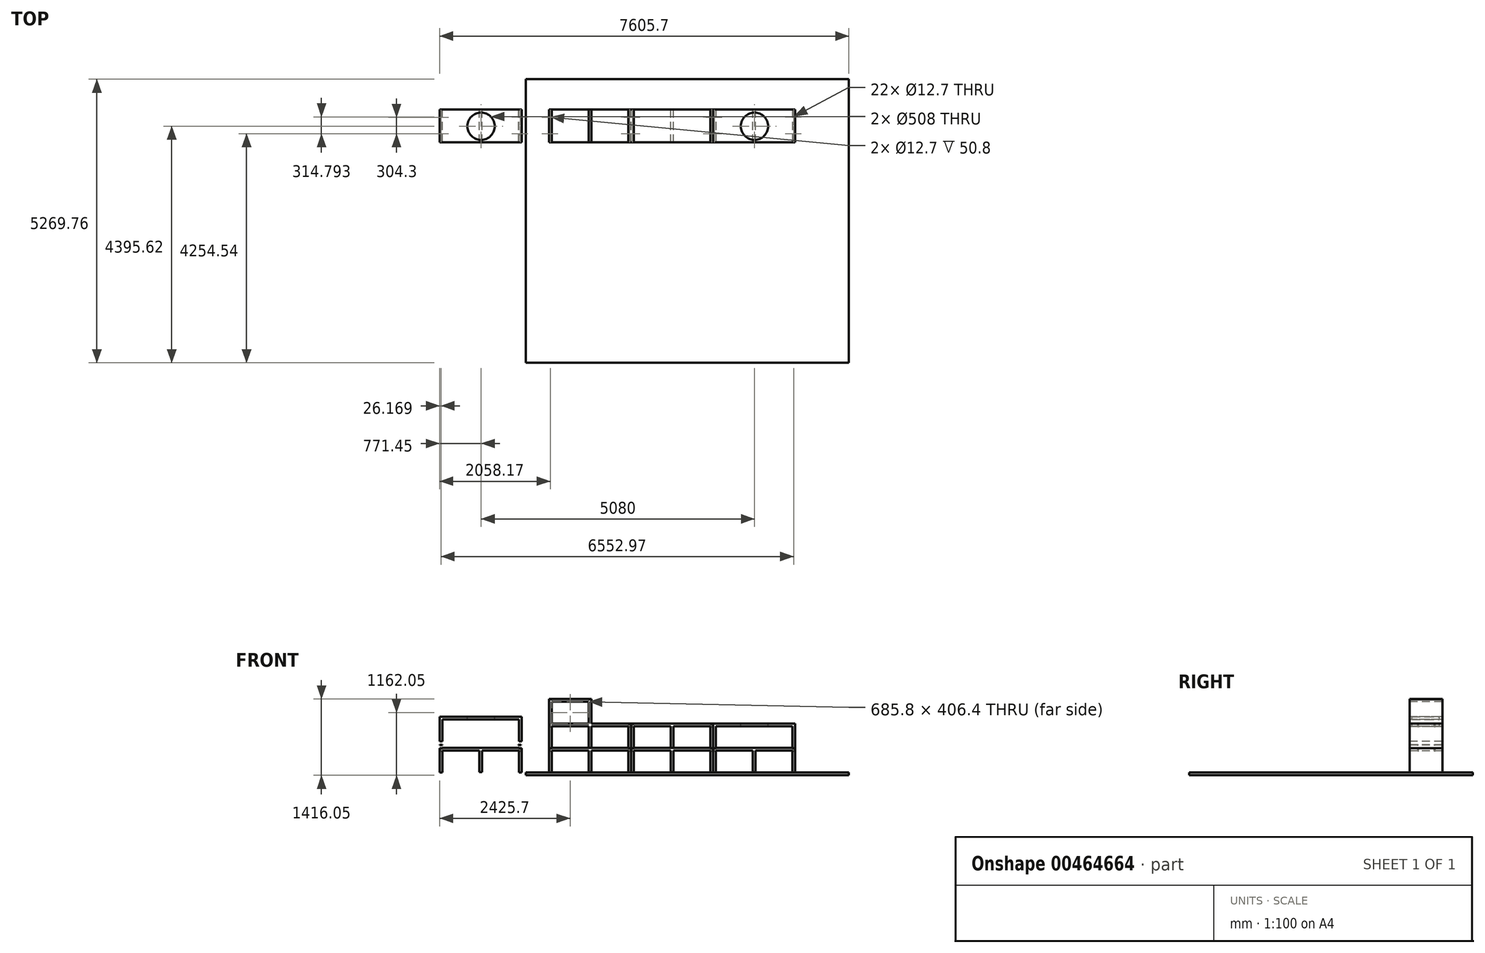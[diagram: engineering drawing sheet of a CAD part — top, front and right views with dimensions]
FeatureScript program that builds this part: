
annotation { "Feature Type Name" : "Feature", "Feature Type Description" : "" }
export const myFeature = defineFeature(function(context is Context, id is Id, definition is map)
    precondition{}
    {
        {
            var Q0;
            Q0=qCreatedBy(makeId("Front.planeOp"),FACE);
            var sketch = newSketch(context, id + "F0", { "sketchPlane" : qUnion([Q0])});
            skLineSegment(sketch, "E0", {"start": v(-136.8, -22.2) * mm, "end": v(-136.8, 33.81) * mm});
            skLineSegment(sketch, "E1", {"start": v(-110.83, 105.81) * mm, "end": v(-110.83, 556.66) * mm});
            skLineSegment(sketch, "E2", {"start": v(-110.83, 556.66) * mm, "end": v(-60.03, 556.66) * mm});
            skLineSegment(sketch, "E3", {"start": v(-60.03, 556.66) * mm, "end": v(-60.03, 563.01) * mm});
            skLineSegment(sketch, "E4", {"start": v(-60.03, 563.01) * mm, "end": v(1362.37, 563.01) * mm});
            skLineSegment(sketch, "E5", {"start": v(1362.37, 563.01) * mm, "end": v(1362.37, 556.66) * mm});
            skLineSegment(sketch, "E6", {"start": v(1362.37, 556.66) * mm, "end": v(1413.17, 556.66) * mm});
            skLineSegment(sketch, "E7", {"start": v(1413.17, 556.66) * mm, "end": v(1413.17, 105.81) * mm});
            skLineSegment(sketch, "E8", {"start": v(1413.17, 105.81) * mm, "end": v(1362.37, 105.81) * mm});
            skLineSegment(sketch, "E9", {"start": v(1362.37, 105.81) * mm, "end": v(1362.37, 512.21) * mm});
            skLineSegment(sketch, "E10", {"start": v(1362.37, 512.21) * mm, "end": v(676.57, 512.21) * mm});
            skLineSegment(sketch, "E11", {"start": v(676.57, 512.21) * mm, "end": v(676.57, 112.16) * mm});
            skLineSegment(sketch, "E12", {"start": v(676.57, 112.16) * mm, "end": v(625.77, 112.16) * mm});
            skLineSegment(sketch, "E13", {"start": v(625.77, 112.16) * mm, "end": v(625.77, 512.21) * mm});
            skLineSegment(sketch, "E14", {"start": v(625.77, 512.21) * mm, "end": v(-60.03, 512.21) * mm});
            skLineSegment(sketch, "E15", {"start": v(-60.03, 512.21) * mm, "end": v(-60.03, 105.81) * mm});
            skLineSegment(sketch, "E16", {"start": v(-60.03, 105.81) * mm, "end": v(-110.83, 105.81) * mm});
            skSolve(sketch);
        }
        {
            var Q0;
            Q0 = qSketchRegion(id + "F0", true);
            extrude(context, id + "F1", {"entities" : qUnion([Q0]), "depth" : 609.6 * mm});
        }
        {
            var Q0;
            Q0=makeQuery(id+"F1.opExtrude","SWEPT_FACE",FACE,{"disambiguationData":[OSD([sQuery(id+"F0.wireOp",EDGE,"E6")])]});
            var sketch = newSketch(context, id + "F2", { "sketchPlane" : qUnion([Q0])});
            skPoint(sketch, "E17", {"position": v(1388.3, -450.4) * mm});
            skPoint(sketch, "E18", {"position": v(1388.3, -135.6) * mm});
            skPoint(sketch, "E19", {"position": v(-84.66, -450.4) * mm});
            skPoint(sketch, "E20", {"position": v(-84.66, -146.1) * mm});
            skSolve(sketch);
        }
        {
            var Q0;
            Q0=sQuery(id+"F2.wireOp",VERTEX,"E20");
            var Q1;
            Q1=sQuery(id+"F2.wireOp",VERTEX,"E19");
            var Q2;
            Q2=sQuery(id+"F2.wireOp",VERTEX,"E18");
            var Q3;
            Q3=sQuery(id+"F2.wireOp",VERTEX,"E17");
            var Q4;
            Q4=makeQuery(id+"F1.opExtrude","SWEPT_BODY",BODY,{"disambiguationData":[OSD([sQuery(id+"F0.wireOp",EDGE,"E1"),sQuery(id+"F0.wireOp",EDGE,"E2"),sQuery(id+"F0.wireOp",EDGE,"E3"),sQuery(id+"F0.wireOp",EDGE,"E4"),sQuery(id+"F0.wireOp",EDGE,"E5"),sQuery(id+"F0.wireOp",EDGE,"E6"),sQuery(id+"F0.wireOp",EDGE,"E7"),sQuery(id+"F0.wireOp",EDGE,"E8"),sQuery(id+"F0.wireOp",EDGE,"E9"),sQuery(id+"F0.wireOp",EDGE,"E10"),sQuery(id+"F0.wireOp",EDGE,"E11"),sQuery(id+"F0.wireOp",EDGE,"E12"),sQuery(id+"F0.wireOp",EDGE,"E13"),sQuery(id+"F0.wireOp",EDGE,"E14"),sQuery(id+"F0.wireOp",EDGE,"E15"),sQuery(id+"F0.wireOp",EDGE,"E16")])]});
            hole(context, id + "F3", {"style" : HoleStyle.SIMPLE, "endStyle" : HoleEndStyle.BLIND, "holeDiameter" : 12.7 * mm, "holeDepth" : 50.8 * mm, "isTappedThrough" : true, "tappedDepth" : 12.7 * mm, "tapClearance" : 3, "locations" : qUnion([Q0, Q1, Q2, Q3]), "scope" : qUnion([Q4])});
        }
        {
            var Q0;
            Q0=makeQuery(id+"F1.opExtrude","CAP_FACE",FACE,{"disambiguationData":[OSD([sQuery(id+"F0.wireOp",EDGE,"E1"),sQuery(id+"F0.wireOp",EDGE,"E2"),sQuery(id+"F0.wireOp",EDGE,"E3"),sQuery(id+"F0.wireOp",EDGE,"E4"),sQuery(id+"F0.wireOp",EDGE,"E5"),sQuery(id+"F0.wireOp",EDGE,"E6"),sQuery(id+"F0.wireOp",EDGE,"E7"),sQuery(id+"F0.wireOp",EDGE,"E8"),sQuery(id+"F0.wireOp",EDGE,"E9"),sQuery(id+"F0.wireOp",EDGE,"E10"),sQuery(id+"F0.wireOp",EDGE,"E11"),sQuery(id+"F0.wireOp",EDGE,"E12"),sQuery(id+"F0.wireOp",EDGE,"E13"),sQuery(id+"F0.wireOp",EDGE,"E14"),sQuery(id+"F0.wireOp",EDGE,"E15"),sQuery(id+"F0.wireOp",EDGE,"E16")])],"isStart":false});
            var sketch = newSketch(context, id + "F4", { "sketchPlane" : qUnion([Q0])});
            skLineSegment(sketch, "E21.bottom", {"start": v(-60.03, 614.6) * mm, "end": v(-110.83, 614.6) * mm});
            skLineSegment(sketch, "E21.top", {"start": v(-60.03, 620.95) * mm, "end": v(-110.83, 620.95) * mm});
            skLineSegment(sketch, "E21.left", {"start": v(-60.03, 614.6) * mm, "end": v(-60.03, 620.95) * mm});
            skLineSegment(sketch, "E21.right", {"start": v(-110.83, 614.6) * mm, "end": v(-110.83, 620.95) * mm});
            skLineSegment(sketch, "E22.bottom", {"start": v(1354.2, 620.95) * mm, "end": v(1405, 620.95) * mm});
            skLineSegment(sketch, "E22.top", {"start": v(1354.2, 614.6) * mm, "end": v(1405, 614.6) * mm});
            skLineSegment(sketch, "E22.left", {"start": v(1354.2, 620.95) * mm, "end": v(1354.2, 614.6) * mm});
            skLineSegment(sketch, "E22.right", {"start": v(1405, 620.95) * mm, "end": v(1405, 614.6) * mm});
            skSolve(sketch);
        }
        {
            var Q0;
            Q0 = qSketchRegion(id + "F4", true);
            extrude(context, id + "F5", {"entities" : qUnion([Q0]), "depth" : -609.6 * mm});
        }
        {
            var Q0;
            Q0=makeQuery(id+"F5.opExtrude","SWEPT_FACE",FACE,{"disambiguationData":[OSD([sQuery(id+"F4.wireOp",EDGE,"E21.top")])]});
            var sketch = newSketch(context, id + "F6", { "sketchPlane" : qUnion([Q0])});
            skPoint(sketch, "E23", {"position": v(-84.4, -137.65) * mm});
            skPoint(sketch, "E24", {"position": v(-84.4, -453.82) * mm});
            skSolve(sketch);
        }
        {
            var Q0;
            Q0=sQuery(id+"F6.wireOp",VERTEX,"E23");
            var Q1;
            Q1=sQuery(id+"F6.wireOp",VERTEX,"E24");
            var Q2;
            Q2=makeQuery(id+"F5.opExtrude","SWEPT_BODY",BODY,{"disambiguationData":[OSD([sQuery(id+"F4.wireOp",EDGE,"E21.bottom"),sQuery(id+"F4.wireOp",EDGE,"E21.top"),sQuery(id+"F4.wireOp",EDGE,"E21.left"),sQuery(id+"F4.wireOp",EDGE,"E21.right")])]});
            hole(context, id + "F7", {"style" : HoleStyle.SIMPLE, "endStyle" : HoleEndStyle.BLIND, "holeDiameter" : 6.35 * mm, "holeDepth" : 6.35 * mm, "isTappedThrough" : true, "tappedDepth" : 12.7 * mm, "tapClearance" : 3, "locations" : qUnion([Q0, Q1]), "scope" : qUnion([Q2])});
        }
        {
            var Q0;
            Q0=makeQuery(id+"F5.opExtrude","SWEPT_FACE",FACE,{"disambiguationData":[OSD([sQuery(id+"F4.wireOp",EDGE,"E22.bottom")])]});
            var sketch = newSketch(context, id + "F8", { "sketchPlane" : qUnion([Q0])});
            skPoint(sketch, "E25", {"position": v(1380.3, -144.1) * mm});
            skPoint(sketch, "E26", {"position": v(1380.3, -466.73) * mm});
            skSolve(sketch);
        }
        {
            var Q0;
            Q0=sQuery(id+"F8.wireOp",VERTEX,"E25");
            var Q1;
            Q1=sQuery(id+"F8.wireOp",VERTEX,"E26");
            var Q2;
            Q2=makeQuery(id+"F5.opExtrude","SWEPT_BODY",BODY,{"disambiguationData":[OSD([sQuery(id+"F4.wireOp",EDGE,"E22.bottom"),sQuery(id+"F4.wireOp",EDGE,"E22.top"),sQuery(id+"F4.wireOp",EDGE,"E22.left"),sQuery(id+"F4.wireOp",EDGE,"E22.right")])]});
            hole(context, id + "F9", {"style" : HoleStyle.SIMPLE, "endStyle" : HoleEndStyle.BLIND, "holeDiameter" : 6.35 * mm, "holeDepth" : 6.35 * mm, "isTappedThrough" : true, "tappedDepth" : 12.7 * mm, "tapClearance" : 3, "locations" : qUnion([Q0, Q1]), "scope" : qUnion([Q2])});
        }
        {
            var Q0;
            Q0=makeQuery(id+"F1.opExtrude","CAP_FACE",FACE,{"disambiguationData":[OSD([sQuery(id+"F0.wireOp",EDGE,"E1"),sQuery(id+"F0.wireOp",EDGE,"E2"),sQuery(id+"F0.wireOp",EDGE,"E3"),sQuery(id+"F0.wireOp",EDGE,"E4"),sQuery(id+"F0.wireOp",EDGE,"E5"),sQuery(id+"F0.wireOp",EDGE,"E6"),sQuery(id+"F0.wireOp",EDGE,"E7"),sQuery(id+"F0.wireOp",EDGE,"E8"),sQuery(id+"F0.wireOp",EDGE,"E9"),sQuery(id+"F0.wireOp",EDGE,"E10"),sQuery(id+"F0.wireOp",EDGE,"E11"),sQuery(id+"F0.wireOp",EDGE,"E12"),sQuery(id+"F0.wireOp",EDGE,"E13"),sQuery(id+"F0.wireOp",EDGE,"E14"),sQuery(id+"F0.wireOp",EDGE,"E15"),sQuery(id+"F0.wireOp",EDGE,"E16")])],"isStart":false});
            var sketch = newSketch(context, id + "F10", { "sketchPlane" : qUnion([Q0])});
            skLineSegment(sketch, "E27", {"start": v(-110.83, 683.85) * mm, "end": v(-110.83, 1141.05) * mm});
            skLineSegment(sketch, "E28", {"start": v(-110.83, 1141.05) * mm, "end": v(1413.17, 1141.05) * mm});
            skLineSegment(sketch, "E29", {"start": v(1413.17, 1141.05) * mm, "end": v(1413.17, 683.85) * mm});
            skLineSegment(sketch, "E30", {"start": v(1413.17, 683.85) * mm, "end": v(1362.37, 683.85) * mm});
            skLineSegment(sketch, "E31", {"start": v(1362.37, 683.85) * mm, "end": v(1362.37, 1090.25) * mm});
            skLineSegment(sketch, "E32", {"start": v(1362.37, 1090.25) * mm, "end": v(-60.03, 1090.25) * mm});
            skLineSegment(sketch, "E33", {"start": v(-60.03, 1090.25) * mm, "end": v(-60.03, 683.85) * mm});
            skLineSegment(sketch, "E34", {"start": v(-60.03, 683.85) * mm, "end": v(-110.83, 683.85) * mm});
            skSolve(sketch);
        }
        {
            var Q0;
            Q0 = qSketchRegion(id + "F10", true);
            extrude(context, id + "F11", {"entities" : qUnion([Q0]), "depth" : -609.6 * mm});
        }
        {
            var Q0;
            Q0=makeQuery(id+"F11.opExtrude","SWEPT_FACE",FACE,{"disambiguationData":[OSD([sQuery(id+"F10.wireOp",EDGE,"E28")])]});
            var sketch = newSketch(context, id + "F12", { "sketchPlane" : qUnion([Q0])});
            skPoint(sketch, "E35", {"position": v(660.62, -309.31) * mm});
            skSolve(sketch);
        }
        {
            var Q0;
            Q0=sQuery(id+"F12.wireOp",VERTEX,"E35");
            var Q1;
            Q1=makeQuery(id+"F11.opExtrude","SWEPT_BODY",BODY,{"disambiguationData":[OSD([sQuery(id+"F10.wireOp",EDGE,"E27"),sQuery(id+"F10.wireOp",EDGE,"E28"),sQuery(id+"F10.wireOp",EDGE,"E29"),sQuery(id+"F10.wireOp",EDGE,"E30"),sQuery(id+"F10.wireOp",EDGE,"E31"),sQuery(id+"F10.wireOp",EDGE,"E32"),sQuery(id+"F10.wireOp",EDGE,"E33"),sQuery(id+"F10.wireOp",EDGE,"E34")])]});
            hole(context, id + "F13", {"style" : HoleStyle.SIMPLE, "endStyle" : HoleEndStyle.BLIND, "holeDiameter" : 508 * mm, "holeDepth" : 50.8 * mm, "isTappedThrough" : true, "tappedDepth" : 12.7 * mm, "tapClearance" : 3, "locations" : qUnion([Q0]), "scope" : qUnion([Q1])});
        }
        {
            var Q0;
            Q0=makeQuery(id+"F1.opExtrude","SWEPT_BODY",BODY,{"disambiguationData":[OSD([sQuery(id+"F0.wireOp",EDGE,"E1"),sQuery(id+"F0.wireOp",EDGE,"E2"),sQuery(id+"F0.wireOp",EDGE,"E3"),sQuery(id+"F0.wireOp",EDGE,"E4"),sQuery(id+"F0.wireOp",EDGE,"E5"),sQuery(id+"F0.wireOp",EDGE,"E6"),sQuery(id+"F0.wireOp",EDGE,"E7"),sQuery(id+"F0.wireOp",EDGE,"E8"),sQuery(id+"F0.wireOp",EDGE,"E9"),sQuery(id+"F0.wireOp",EDGE,"E10"),sQuery(id+"F0.wireOp",EDGE,"E11"),sQuery(id+"F0.wireOp",EDGE,"E12"),sQuery(id+"F0.wireOp",EDGE,"E13"),sQuery(id+"F0.wireOp",EDGE,"E14"),sQuery(id+"F0.wireOp",EDGE,"E15"),sQuery(id+"F0.wireOp",EDGE,"E16")])]});
            transform(context, id + "F14", {"entities" : qUnion([Q0]), "transformType" : TransformType.TRANSLATION_3D, "dx" : 2032 * mm, "dy" : 0 * mm, "dz" : 0 * mm, "makeCopy" : true});
        }
        {
            var Q0;
            Q0=makeQuery(id+"F14.opPattern","COPY",BODY,{"derivedFrom":makeQuery(id+"F1.opExtrude","SWEPT_BODY",BODY,{"disambiguationData":[OSD([sQuery(id+"F0.wireOp",EDGE,"E1"),sQuery(id+"F0.wireOp",EDGE,"E2"),sQuery(id+"F0.wireOp",EDGE,"E3"),sQuery(id+"F0.wireOp",EDGE,"E4"),sQuery(id+"F0.wireOp",EDGE,"E5"),sQuery(id+"F0.wireOp",EDGE,"E6"),sQuery(id+"F0.wireOp",EDGE,"E7"),sQuery(id+"F0.wireOp",EDGE,"E8"),sQuery(id+"F0.wireOp",EDGE,"E9"),sQuery(id+"F0.wireOp",EDGE,"E10"),sQuery(id+"F0.wireOp",EDGE,"E11"),sQuery(id+"F0.wireOp",EDGE,"E12"),sQuery(id+"F0.wireOp",EDGE,"E13"),sQuery(id+"F0.wireOp",EDGE,"E14"),sQuery(id+"F0.wireOp",EDGE,"E15"),sQuery(id+"F0.wireOp",EDGE,"E16")])]}),"instanceName":"1"});
            transform(context, id + "F15", {"entities" : qUnion([Q0]), "transformType" : TransformType.TRANSLATION_3D, "dx" : 0 * mm, "dy" : 0 * mm, "dz" : 450.85 * mm, "makeCopy" : true});
        }
        {
            var Q0;
            Q0=makeQuery(id+"F14.opPattern","COPY",BODY,{"derivedFrom":makeQuery(id+"F1.opExtrude","SWEPT_BODY",BODY,{"disambiguationData":[OSD([sQuery(id+"F0.wireOp",EDGE,"E1"),sQuery(id+"F0.wireOp",EDGE,"E2"),sQuery(id+"F0.wireOp",EDGE,"E3"),sQuery(id+"F0.wireOp",EDGE,"E4"),sQuery(id+"F0.wireOp",EDGE,"E5"),sQuery(id+"F0.wireOp",EDGE,"E6"),sQuery(id+"F0.wireOp",EDGE,"E7"),sQuery(id+"F0.wireOp",EDGE,"E8"),sQuery(id+"F0.wireOp",EDGE,"E9"),sQuery(id+"F0.wireOp",EDGE,"E10"),sQuery(id+"F0.wireOp",EDGE,"E11"),sQuery(id+"F0.wireOp",EDGE,"E12"),sQuery(id+"F0.wireOp",EDGE,"E13"),sQuery(id+"F0.wireOp",EDGE,"E14"),sQuery(id+"F0.wireOp",EDGE,"E15"),sQuery(id+"F0.wireOp",EDGE,"E16")])]}),"instanceName":"1"});
            transform(context, id + "F16", {"entities" : qUnion([Q0]), "transformType" : TransformType.TRANSLATION_3D, "dx" : 1524 * mm, "dy" : 0 * mm, "dz" : 0 * mm, "makeCopy" : true});
        }
        {
            var Q0;
            Q0=makeQuery(id+"F15.opPattern","COPY",BODY,{"derivedFrom":makeQuery(id+"F14.opPattern","COPY",BODY,{"derivedFrom":makeQuery(id+"F1.opExtrude","SWEPT_BODY",BODY,{"disambiguationData":[OSD([sQuery(id+"F0.wireOp",EDGE,"E1"),sQuery(id+"F0.wireOp",EDGE,"E2"),sQuery(id+"F0.wireOp",EDGE,"E3"),sQuery(id+"F0.wireOp",EDGE,"E4"),sQuery(id+"F0.wireOp",EDGE,"E5"),sQuery(id+"F0.wireOp",EDGE,"E6"),sQuery(id+"F0.wireOp",EDGE,"E7"),sQuery(id+"F0.wireOp",EDGE,"E8"),sQuery(id+"F0.wireOp",EDGE,"E9"),sQuery(id+"F0.wireOp",EDGE,"E10"),sQuery(id+"F0.wireOp",EDGE,"E11"),sQuery(id+"F0.wireOp",EDGE,"E12"),sQuery(id+"F0.wireOp",EDGE,"E13"),sQuery(id+"F0.wireOp",EDGE,"E14"),sQuery(id+"F0.wireOp",EDGE,"E15"),sQuery(id+"F0.wireOp",EDGE,"E16")])]}),"instanceName":"1"}),"instanceName":"1"});
            transform(context, id + "F17", {"entities" : qUnion([Q0]), "transformType" : TransformType.TRANSLATION_3D, "dx" : 1524 * mm, "dy" : 0 * mm, "dz" : 0 * mm, "makeCopy" : true});
        }
        {
            var Q0;
            Q0=makeQuery(id+"F16.opPattern","COPY",BODY,{"derivedFrom":makeQuery(id+"F14.opPattern","COPY",BODY,{"derivedFrom":makeQuery(id+"F1.opExtrude","SWEPT_BODY",BODY,{"disambiguationData":[OSD([sQuery(id+"F0.wireOp",EDGE,"E1"),sQuery(id+"F0.wireOp",EDGE,"E2"),sQuery(id+"F0.wireOp",EDGE,"E3"),sQuery(id+"F0.wireOp",EDGE,"E4"),sQuery(id+"F0.wireOp",EDGE,"E5"),sQuery(id+"F0.wireOp",EDGE,"E6"),sQuery(id+"F0.wireOp",EDGE,"E7"),sQuery(id+"F0.wireOp",EDGE,"E8"),sQuery(id+"F0.wireOp",EDGE,"E9"),sQuery(id+"F0.wireOp",EDGE,"E10"),sQuery(id+"F0.wireOp",EDGE,"E11"),sQuery(id+"F0.wireOp",EDGE,"E12"),sQuery(id+"F0.wireOp",EDGE,"E13"),sQuery(id+"F0.wireOp",EDGE,"E14"),sQuery(id+"F0.wireOp",EDGE,"E15"),sQuery(id+"F0.wireOp",EDGE,"E16")])]}),"instanceName":"1"}),"instanceName":"1"});
            transform(context, id + "F18", {"entities" : qUnion([Q0]), "transformType" : TransformType.TRANSLATION_3D, "dx" : 1524 * mm, "dy" : 0 * mm, "dz" : 0 * mm, "makeCopy" : true});
        }
        {
            var Q0;
            Q0=makeQuery(id+"F11.opExtrude","SWEPT_BODY",BODY,{"disambiguationData":[OSD([sQuery(id+"F10.wireOp",EDGE,"E27"),sQuery(id+"F10.wireOp",EDGE,"E28"),sQuery(id+"F10.wireOp",EDGE,"E29"),sQuery(id+"F10.wireOp",EDGE,"E30"),sQuery(id+"F10.wireOp",EDGE,"E31"),sQuery(id+"F10.wireOp",EDGE,"E32"),sQuery(id+"F10.wireOp",EDGE,"E33"),sQuery(id+"F10.wireOp",EDGE,"E34")])]});
            transform(context, id + "F19", {"entities" : qUnion([Q0]), "transformType" : TransformType.TRANSLATION_3D, "dx" : 5080 * mm, "dy" : 0 * mm, "dz" : -127 * mm, "makeCopy" : true});
        }
        {
            var Q0;
            Q0=makeQuery(id+"F15.opPattern","COPY",FACE,{"derivedFrom":makeQuery(id+"F14.opPattern","COPY",FACE,{"derivedFrom":makeQuery(id+"F1.opExtrude","CAP_FACE",FACE,{"disambiguationData":[OSD([sQuery(id+"F0.wireOp",EDGE,"E1"),sQuery(id+"F0.wireOp",EDGE,"E2"),sQuery(id+"F0.wireOp",EDGE,"E3"),sQuery(id+"F0.wireOp",EDGE,"E4"),sQuery(id+"F0.wireOp",EDGE,"E5"),sQuery(id+"F0.wireOp",EDGE,"E6"),sQuery(id+"F0.wireOp",EDGE,"E7"),sQuery(id+"F0.wireOp",EDGE,"E8"),sQuery(id+"F0.wireOp",EDGE,"E9"),sQuery(id+"F0.wireOp",EDGE,"E10"),sQuery(id+"F0.wireOp",EDGE,"E11"),sQuery(id+"F0.wireOp",EDGE,"E12"),sQuery(id+"F0.wireOp",EDGE,"E13"),sQuery(id+"F0.wireOp",EDGE,"E14"),sQuery(id+"F0.wireOp",EDGE,"E15"),sQuery(id+"F0.wireOp",EDGE,"E16")])],"isStart":false}),"instanceName":"1"}),"instanceName":"1"});
            var sketch = newSketch(context, id + "F20", { "sketchPlane" : qUnion([Q0])});
            skLineSegment(sketch, "E36.bottom", {"start": v(3394.37, 1007.51) * mm, "end": v(3495.71, 1007.51) * mm});
            skLineSegment(sketch, "E36.top", {"start": v(3394.37, 1013.86) * mm, "end": v(3495.71, 1013.86) * mm});
            skLineSegment(sketch, "E36.left", {"start": v(3394.37, 1007.51) * mm, "end": v(3394.37, 1013.86) * mm});
            skLineSegment(sketch, "E36.right", {"start": v(3495.71, 1007.51) * mm, "end": v(3495.71, 1013.86) * mm});
            skSolve(sketch);
        }
        {
            var Q0;
            Q0=sQuery(id+"F20.wireOp",EDGE,"E36.bottom");
            extrude(context, id + "F21", {"bodyType" : ToolBodyType.SURFACE, "surfaceEntities" : qUnion([Q0]), "depth" : -609.6 * mm});
        }
        {
            var Q0;
            Q0=makeQuery(id+"F19.opPattern","COPY",BODY,{"derivedFrom":makeQuery(id+"F11.opExtrude","SWEPT_BODY",BODY,{"disambiguationData":[OSD([sQuery(id+"F10.wireOp",EDGE,"E27"),sQuery(id+"F10.wireOp",EDGE,"E28"),sQuery(id+"F10.wireOp",EDGE,"E29"),sQuery(id+"F10.wireOp",EDGE,"E30"),sQuery(id+"F10.wireOp",EDGE,"E31"),sQuery(id+"F10.wireOp",EDGE,"E32"),sQuery(id+"F10.wireOp",EDGE,"E33"),sQuery(id+"F10.wireOp",EDGE,"E34")])]}),"instanceName":"1"});
            deleteBodies(context, id + "F22", {"entities" : qUnion([Q0])});
        }
        {
            var Q0;
            Q0=makeQuery(id+"F15.opPattern","COPY",FACE,{"derivedFrom":makeQuery(id+"F14.opPattern","COPY",FACE,{"derivedFrom":makeQuery(id+"F1.opExtrude","CAP_FACE",FACE,{"disambiguationData":[OSD([sQuery(id+"F0.wireOp",EDGE,"E1"),sQuery(id+"F0.wireOp",EDGE,"E2"),sQuery(id+"F0.wireOp",EDGE,"E3"),sQuery(id+"F0.wireOp",EDGE,"E4"),sQuery(id+"F0.wireOp",EDGE,"E5"),sQuery(id+"F0.wireOp",EDGE,"E6"),sQuery(id+"F0.wireOp",EDGE,"E7"),sQuery(id+"F0.wireOp",EDGE,"E8"),sQuery(id+"F0.wireOp",EDGE,"E9"),sQuery(id+"F0.wireOp",EDGE,"E10"),sQuery(id+"F0.wireOp",EDGE,"E11"),sQuery(id+"F0.wireOp",EDGE,"E12"),sQuery(id+"F0.wireOp",EDGE,"E13"),sQuery(id+"F0.wireOp",EDGE,"E14"),sQuery(id+"F0.wireOp",EDGE,"E15"),sQuery(id+"F0.wireOp",EDGE,"E16")])],"isStart":false}),"instanceName":"1"}),"instanceName":"1"});
            var sketch = newSketch(context, id + "F23", { "sketchPlane" : qUnion([Q0])});
            skLineSegment(sketch, "E37.bottom", {"start": v(3394.37, 1007.51) * mm, "end": v(3495.71, 1007.51) * mm});
            skLineSegment(sketch, "E37.top", {"start": v(3394.37, 1013.86) * mm, "end": v(3495.71, 1013.86) * mm});
            skLineSegment(sketch, "E37.left", {"start": v(3394.37, 1007.51) * mm, "end": v(3394.37, 1013.86) * mm});
            skLineSegment(sketch, "E37.right", {"start": v(3495.71, 1007.51) * mm, "end": v(3495.71, 1013.86) * mm});
            skSolve(sketch);
        }
        {
            var Q0;
            Q0 = qSketchRegion(id + "F23", true);
            extrude(context, id + "F24", {"entities" : qUnion([Q0]), "depth" : -609.6 * mm});
        }
        {
            var Q0;
            Q0=makeQuery(id+"F15.opPattern","COPY",FACE,{"derivedFrom":makeQuery(id+"F14.opPattern","COPY",FACE,{"derivedFrom":makeQuery(id+"F1.opExtrude","CAP_FACE",FACE,{"disambiguationData":[OSD([sQuery(id+"F0.wireOp",EDGE,"E1"),sQuery(id+"F0.wireOp",EDGE,"E2"),sQuery(id+"F0.wireOp",EDGE,"E3"),sQuery(id+"F0.wireOp",EDGE,"E4"),sQuery(id+"F0.wireOp",EDGE,"E5"),sQuery(id+"F0.wireOp",EDGE,"E6"),sQuery(id+"F0.wireOp",EDGE,"E7"),sQuery(id+"F0.wireOp",EDGE,"E8"),sQuery(id+"F0.wireOp",EDGE,"E9"),sQuery(id+"F0.wireOp",EDGE,"E10"),sQuery(id+"F0.wireOp",EDGE,"E11"),sQuery(id+"F0.wireOp",EDGE,"E12"),sQuery(id+"F0.wireOp",EDGE,"E13"),sQuery(id+"F0.wireOp",EDGE,"E14"),sQuery(id+"F0.wireOp",EDGE,"E15"),sQuery(id+"F0.wireOp",EDGE,"E16")])],"isStart":false}),"instanceName":"1"}),"instanceName":"1"});
            var sketch = newSketch(context, id + "F25", { "sketchPlane" : qUnion([Q0])});
            skLineSegment(sketch, "E38.bottom", {"start": v(1971.97, 1013.86) * mm, "end": v(1921.17, 1013.86) * mm});
            skLineSegment(sketch, "E38.top", {"start": v(1971.97, 1007.51) * mm, "end": v(1921.17, 1007.51) * mm});
            skLineSegment(sketch, "E38.left", {"start": v(1971.97, 1013.86) * mm, "end": v(1971.97, 1007.51) * mm});
            skLineSegment(sketch, "E38.right", {"start": v(1921.17, 1013.86) * mm, "end": v(1921.17, 1007.51) * mm});
            skSolve(sketch);
        }
        {
            var Q0;
            Q0 = qSketchRegion(id + "F25", true);
            extrude(context, id + "F26", {"entities" : qUnion([Q0]), "operationType" : NewBodyOperationType.ADD, "depth" : -609.6 * mm});
        }
        {
            var Q0;
            Q0=makeQuery(id+"F11.opExtrude","SWEPT_BODY",BODY,{"disambiguationData":[OSD([sQuery(id+"F10.wireOp",EDGE,"E27"),sQuery(id+"F10.wireOp",EDGE,"E28"),sQuery(id+"F10.wireOp",EDGE,"E29"),sQuery(id+"F10.wireOp",EDGE,"E30"),sQuery(id+"F10.wireOp",EDGE,"E31"),sQuery(id+"F10.wireOp",EDGE,"E32"),sQuery(id+"F10.wireOp",EDGE,"E33"),sQuery(id+"F10.wireOp",EDGE,"E34")])]});
            transform(context, id + "F27", {"entities" : qUnion([Q0]), "transformType" : TransformType.TRANSLATION_3D, "dx" : 5080 * mm, "dy" : 0 * mm, "dz" : -127 * mm, "makeCopy" : true});
        }
        {
            var Q0;
            Q0=makeQuery(id+"F1.opExtrude","CAP_FACE",FACE,{"disambiguationData":[OSD([sQuery(id+"F0.wireOp",EDGE,"E1"),sQuery(id+"F0.wireOp",EDGE,"E2"),sQuery(id+"F0.wireOp",EDGE,"E3"),sQuery(id+"F0.wireOp",EDGE,"E4"),sQuery(id+"F0.wireOp",EDGE,"E5"),sQuery(id+"F0.wireOp",EDGE,"E6"),sQuery(id+"F0.wireOp",EDGE,"E7"),sQuery(id+"F0.wireOp",EDGE,"E8"),sQuery(id+"F0.wireOp",EDGE,"E9"),sQuery(id+"F0.wireOp",EDGE,"E10"),sQuery(id+"F0.wireOp",EDGE,"E11"),sQuery(id+"F0.wireOp",EDGE,"E12"),sQuery(id+"F0.wireOp",EDGE,"E13"),sQuery(id+"F0.wireOp",EDGE,"E14"),sQuery(id+"F0.wireOp",EDGE,"E15"),sQuery(id+"F0.wireOp",EDGE,"E16")])],"isStart":false});
            var sketch = newSketch(context, id + "F28", { "sketchPlane" : qUnion([Q0])});
            skSolve(sketch);
        }
        {
            var Q0;
            Q0=makeQuery(id+"F17.opPattern","COPY",FACE,{"derivedFrom":makeQuery(id+"F15.opPattern","COPY",FACE,{"derivedFrom":makeQuery(id+"F14.opPattern","COPY",FACE,{"derivedFrom":makeQuery(id+"F1.opExtrude","SWEPT_FACE",FACE,{"disambiguationData":[OSD([sQuery(id+"F0.wireOp",EDGE,"E6")])]}),"instanceName":"1"}),"instanceName":"1"}),"instanceName":"1"});
            var sketch = newSketch(context, id + "F29", { "sketchPlane" : qUnion([Q0])});
            skLineSegment(sketch, "E39.bottom", {"start": v(4918.37, 0) * mm, "end": v(4969.17, 0) * mm});
            skLineSegment(sketch, "E39.top", {"start": v(4918.37, -609.6) * mm, "end": v(4969.17, -609.6) * mm});
            skLineSegment(sketch, "E39.left", {"start": v(4918.37, 0) * mm, "end": v(4918.37, -609.6) * mm});
            skLineSegment(sketch, "E39.right", {"start": v(4969.17, 0) * mm, "end": v(4969.17, -609.6) * mm});
            skSolve(sketch);
        }
        {
            var Q0;
            Q0 = qSketchRegion(id + "F29", true);
            extrude(context, id + "F30", {"entities" : qUnion([Q0]), "depth" : 6.35 * mm});
        }
        {
            var Q0;
            Q0=makeQuery(id+"F26.boolean.opBoolean","MERGE",FACE,{"derivedFrom":[makeQuery(id+"F15.opPattern","COPY",FACE,{"derivedFrom":makeQuery(id+"F14.opPattern","COPY",FACE,{"derivedFrom":makeQuery(id+"F1.opExtrude","CAP_FACE",FACE,{"disambiguationData":[OSD([sQuery(id+"F0.wireOp",EDGE,"E1"),sQuery(id+"F0.wireOp",EDGE,"E2"),sQuery(id+"F0.wireOp",EDGE,"E3"),sQuery(id+"F0.wireOp",EDGE,"E4"),sQuery(id+"F0.wireOp",EDGE,"E5"),sQuery(id+"F0.wireOp",EDGE,"E6"),sQuery(id+"F0.wireOp",EDGE,"E7"),sQuery(id+"F0.wireOp",EDGE,"E8"),sQuery(id+"F0.wireOp",EDGE,"E9"),sQuery(id+"F0.wireOp",EDGE,"E10"),sQuery(id+"F0.wireOp",EDGE,"E11"),sQuery(id+"F0.wireOp",EDGE,"E12"),sQuery(id+"F0.wireOp",EDGE,"E13"),sQuery(id+"F0.wireOp",EDGE,"E14"),sQuery(id+"F0.wireOp",EDGE,"E15"),sQuery(id+"F0.wireOp",EDGE,"E16")])],"isStart":false}),"instanceName":"1"}),"instanceName":"1"}),makeQuery(id+"F26.opExtrude","CAP_FACE",FACE,{"disambiguationData":[OSD([sQuery(id+"F25.wireOp",EDGE,"E38.bottom"),sQuery(id+"F25.wireOp",EDGE,"E38.top"),sQuery(id+"F25.wireOp",EDGE,"E38.left"),sQuery(id+"F25.wireOp",EDGE,"E38.right")])],"isStart":true})]});
            var sketch = newSketch(context, id + "F31", { "sketchPlane" : qUnion([Q0])});
            skLineSegment(sketch, "E40", {"start": v(1921.17, 1013.86) * mm, "end": v(1921.17, 1464.71) * mm});
            skLineSegment(sketch, "E41", {"start": v(1921.17, 1464.71) * mm, "end": v(1971.97, 1464.71) * mm});
            skLineSegment(sketch, "E42", {"start": v(1971.97, 1464.71) * mm, "end": v(1971.97, 1471.06) * mm});
            skLineSegment(sketch, "E43", {"start": v(1971.97, 1471.06) * mm, "end": v(2657.77, 1471.06) * mm});
            skLineSegment(sketch, "E44", {"start": v(2657.77, 1471.06) * mm, "end": v(2657.77, 1464.71) * mm});
            skLineSegment(sketch, "E45", {"start": v(2657.77, 1464.71) * mm, "end": v(2708.57, 1464.71) * mm});
            skLineSegment(sketch, "E46", {"start": v(2708.57, 1464.71) * mm, "end": v(2708.57, 1013.86) * mm});
            skLineSegment(sketch, "E47", {"start": v(2708.57, 1013.86) * mm, "end": v(2657.77, 1013.86) * mm});
            skLineSegment(sketch, "E48", {"start": v(2657.77, 1013.86) * mm, "end": v(2657.77, 1420.26) * mm});
            skLineSegment(sketch, "E49", {"start": v(2657.77, 1420.26) * mm, "end": v(1971.97, 1420.26) * mm});
            skLineSegment(sketch, "E50", {"start": v(1971.97, 1420.26) * mm, "end": v(1971.97, 1013.86) * mm});
            skLineSegment(sketch, "E51", {"start": v(1971.97, 1013.86) * mm, "end": v(1921.17, 1013.86) * mm});
            skSolve(sketch);
        }
        {
            var Q0;
            Q0 = qSketchRegion(id + "F31", true);
            extrude(context, id + "F32", {"entities" : qUnion([Q0]), "operationType" : NewBodyOperationType.ADD, "depth" : -609.6 * mm});
        }
        {
            var Q0;
            Q0=makeQuery(id+"F32.boolean.opBoolean","MERGE",FACE,{"derivedFrom":[makeQuery(id+"F26.boolean.opBoolean","MERGE",FACE,{"derivedFrom":[makeQuery(id+"F15.opPattern","COPY",FACE,{"derivedFrom":makeQuery(id+"F14.opPattern","COPY",FACE,{"derivedFrom":makeQuery(id+"F1.opExtrude","CAP_FACE",FACE,{"disambiguationData":[OSD([sQuery(id+"F0.wireOp",EDGE,"E1"),sQuery(id+"F0.wireOp",EDGE,"E2"),sQuery(id+"F0.wireOp",EDGE,"E3"),sQuery(id+"F0.wireOp",EDGE,"E4"),sQuery(id+"F0.wireOp",EDGE,"E5"),sQuery(id+"F0.wireOp",EDGE,"E6"),sQuery(id+"F0.wireOp",EDGE,"E7"),sQuery(id+"F0.wireOp",EDGE,"E8"),sQuery(id+"F0.wireOp",EDGE,"E9"),sQuery(id+"F0.wireOp",EDGE,"E10"),sQuery(id+"F0.wireOp",EDGE,"E11"),sQuery(id+"F0.wireOp",EDGE,"E12"),sQuery(id+"F0.wireOp",EDGE,"E13"),sQuery(id+"F0.wireOp",EDGE,"E14"),sQuery(id+"F0.wireOp",EDGE,"E15"),sQuery(id+"F0.wireOp",EDGE,"E16")])],"isStart":false}),"instanceName":"1"}),"instanceName":"1"}),makeQuery(id+"F26.opExtrude","CAP_FACE",FACE,{"disambiguationData":[OSD([sQuery(id+"F25.wireOp",EDGE,"E38.bottom"),sQuery(id+"F25.wireOp",EDGE,"E38.top"),sQuery(id+"F25.wireOp",EDGE,"E38.left"),sQuery(id+"F25.wireOp",EDGE,"E38.right")])],"isStart":true})]}),makeQuery(id+"F32.opExtrude","CAP_FACE",FACE,{"disambiguationData":[OSD([sQuery(id+"F31.wireOp",EDGE,"E40"),sQuery(id+"F31.wireOp",EDGE,"E41"),sQuery(id+"F31.wireOp",EDGE,"E42"),sQuery(id+"F31.wireOp",EDGE,"E43"),sQuery(id+"F31.wireOp",EDGE,"E44"),sQuery(id+"F31.wireOp",EDGE,"E45"),sQuery(id+"F31.wireOp",EDGE,"E46"),sQuery(id+"F31.wireOp",EDGE,"E47"),sQuery(id+"F31.wireOp",EDGE,"E48"),sQuery(id+"F31.wireOp",EDGE,"E49"),sQuery(id+"F31.wireOp",EDGE,"E50"),sQuery(id+"F31.wireOp",EDGE,"E51")])],"isStart":true})]});
            var sketch = newSketch(context, id + "F33", { "sketchPlane" : qUnion([Q0])});
            skLineSegment(sketch, "E52.bottom", {"start": v(1861.17, 1464.71) * mm, "end": v(1810.37, 1464.71) * mm});
            skLineSegment(sketch, "E52.top", {"start": v(1861.17, 1471.06) * mm, "end": v(1810.37, 1471.06) * mm});
            skLineSegment(sketch, "E52.left", {"start": v(1861.17, 1464.71) * mm, "end": v(1861.17, 1471.06) * mm});
            skLineSegment(sketch, "E52.right", {"start": v(1810.37, 1464.71) * mm, "end": v(1810.37, 1471.06) * mm});
            skSolve(sketch);
        }
        {
            var Q0;
            Q0 = qSketchRegion(id + "F33", true);
            extrude(context, id + "F34", {"entities" : qUnion([Q0]), "depth" : -609.6 * mm});
        }
        {
            var Q0;
            Q0=makeQuery(id+"F34.opExtrude","SWEPT_BODY",BODY,{"disambiguationData":[OSD([sQuery(id+"F33.wireOp",EDGE,"E52.bottom"),sQuery(id+"F33.wireOp",EDGE,"E52.top"),sQuery(id+"F33.wireOp",EDGE,"E52.left"),sQuery(id+"F33.wireOp",EDGE,"E52.right")])]});
            transform(context, id + "F35", {"entities" : qUnion([Q0]), "transformType" : TransformType.TRANSLATION_3D, "dx" : 110.49 * mm, "dy" : 0 * mm, "dz" : 0 * mm, "makeCopy" : true});
        }
        {
            var Q0;
            Q0=makeQuery(id+"F34.opExtrude","SWEPT_BODY",BODY,{"disambiguationData":[OSD([sQuery(id+"F33.wireOp",EDGE,"E52.bottom"),sQuery(id+"F33.wireOp",EDGE,"E52.top"),sQuery(id+"F33.wireOp",EDGE,"E52.left"),sQuery(id+"F33.wireOp",EDGE,"E52.right")])]});
            deleteBodies(context, id + "F36", {"entities" : qUnion([Q0])});
        }
        {
            var Q0;
            Q0=makeQuery(id+"F35.opPattern","COPY",BODY,{"derivedFrom":makeQuery(id+"F34.opExtrude","SWEPT_BODY",BODY,{"disambiguationData":[OSD([sQuery(id+"F33.wireOp",EDGE,"E52.bottom"),sQuery(id+"F33.wireOp",EDGE,"E52.top"),sQuery(id+"F33.wireOp",EDGE,"E52.left"),sQuery(id+"F33.wireOp",EDGE,"E52.right")])]}),"instanceName":"1"});
            transform(context, id + "F37", {"entities" : qUnion([Q0]), "transformType" : TransformType.TRANSLATION_3D, "dx" : 736.6 * mm, "dy" : 0 * mm, "dz" : 0 * mm, "makeCopy" : true});
        }
        {
            var Q0;
            Q0=makeQuery(id+"F14.opPattern","COPY",FACE,{"derivedFrom":makeQuery(id+"F1.opExtrude","SWEPT_FACE",FACE,{"disambiguationData":[OSD([sQuery(id+"F0.wireOp",EDGE,"E16")])]}),"instanceName":"1"});
            var sketch = newSketch(context, id + "F38", { "sketchPlane" : qUnion([Q0])});
            skLineSegment(sketch, "E53.bottom", {"start": v(7494.87, -564.83) * mm, "end": v(1492.66, -564.83) * mm});
            skLineSegment(sketch, "E53.top", {"start": v(7494.87, 4704.93) * mm, "end": v(1492.66, 4704.93) * mm});
            skLineSegment(sketch, "E53.left", {"start": v(7494.87, -564.83) * mm, "end": v(7494.87, 4704.93) * mm});
            skLineSegment(sketch, "E53.right", {"start": v(1492.66, -564.83) * mm, "end": v(1492.66, 4704.93) * mm});
            skSolve(sketch);
        }
        {
            var Q0;
            Q0 = qSketchRegion(id + "F38", true);
            extrude(context, id + "F39", {"entities" : qUnion([Q0]), "depth" : 50.8 * mm});
        }
    });
